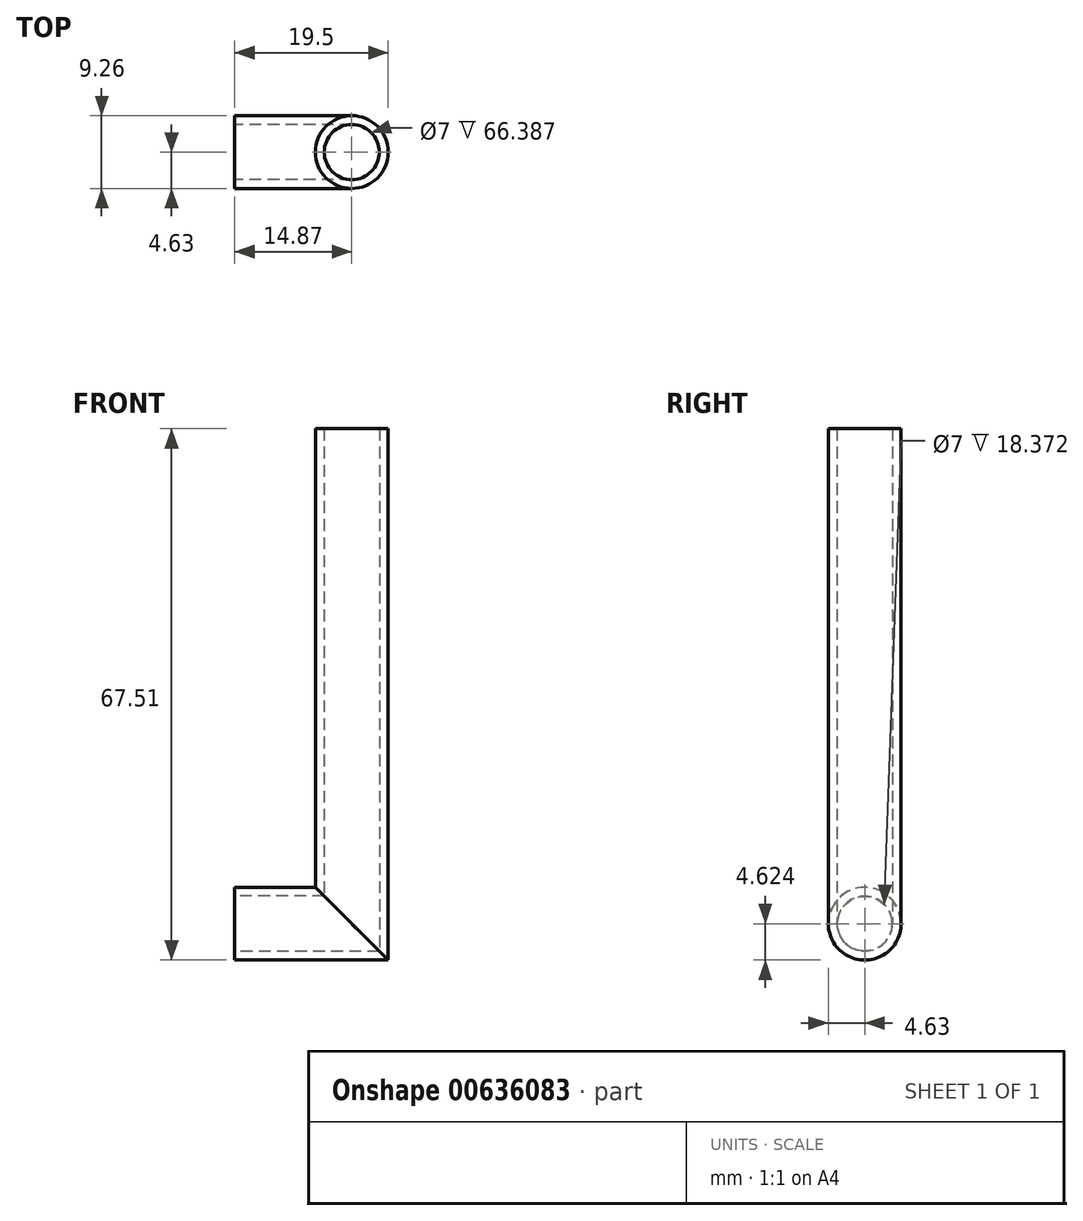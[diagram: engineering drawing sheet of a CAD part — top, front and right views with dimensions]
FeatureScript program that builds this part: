
annotation { "Feature Type Name" : "Feature", "Feature Type Description" : "" }
export const myFeature = defineFeature(function(context is Context, id is Id, definition is map)
    precondition{}
    {
        {
            var Q0;
            Q0=qCreatedBy(makeId("Top.planeOp"),FACE);
            var sketch = newSketch(context, id + "F0", { "sketchPlane" : qUnion([Q0])});
            skCircle(sketch, "E0", {"center": v(0, 0) * mm, "radius": 4.63 * mm});
            skSolve(sketch);
        }
        {
            var Q0;
            Q0=qCreatedBy(makeId("Front.planeOp"),FACE);
            var sketch = newSketch(context, id + "F1", { "sketchPlane" : qUnion([Q0])});
            skLineSegment(sketch, "E1", {"start": v(0, 53.68) * mm, "end": v(0, 0) * mm});
            skLineSegment(sketch, "E2", {"start": v(0, 0) * mm, "end": v(0, -9.2) * mm});
            skLineSegment(sketch, "E3", {"start": v(0, -9.2) * mm, "end": v(-14.87, -9.2) * mm});
            skSolve(sketch);
        }
        {
            var Q0;
            Q0=makeQuery(id+"F0.imprint","IMPRINT",FACE,{"disambiguationData":[TD([[makeQuery(id+"F0.imprint","IMPRINT",EDGE,{"derivedFrom":sQuery(id+"F0.wireOp",EDGE,"E0")}),1.0]])]});
            var Q1;
            Q1=sQuery(id+"F1.wireOp",EDGE,"E3");
            var Q2;
            Q2=sQuery(id+"F1.wireOp",EDGE,"E1");
            var Q3;
            Q3=sQuery(id+"F1.wireOp",EDGE,"E2");
            sweep(context, id + "F2", {"profiles" : qUnion([Q0]), "path" : qUnion([Q1, Q2, Q3])});
        }
        {
            var Q0;
            Q0=makeQuery(id+"F2.opSweep","CAP_FACE",FACE,{"disambiguationData":[OSD([sQuery(id+"F0.wireOp",EDGE,"E0"),sQuery(id+"F1.wireOp",VERTEX,"E1.start")])],"isStart":false});
            var sketch = newSketch(context, id + "F3", { "sketchPlane" : qUnion([Q0])});
            skCircle(sketch, "E4", {"center": v(0, 0) * mm, "radius": 3.5 * mm});
            skSolve(sketch);
        }
        {
            var Q0;
            Q0=makeQuery(id+"F3.imprint","IMPRINT",FACE,{"disambiguationData":[TD([[makeQuery(id+"F3.imprint","IMPRINT",EDGE,{"derivedFrom":sQuery(id+"F3.wireOp",EDGE,"E4")}),1.0]])]});
            var Q1;
            Q1 = qConstructionFilter(qBodyType(qCreatedBy(id + "F1" ,EDGE), BodyType.WIRE), ConstructionObject.NO);
            sweep(context, id + "F4", {"operationType" : NewBodyOperationType.REMOVE, "profiles" : qUnion([Q0]), "path" : qUnion([Q1])});
        }
    });
